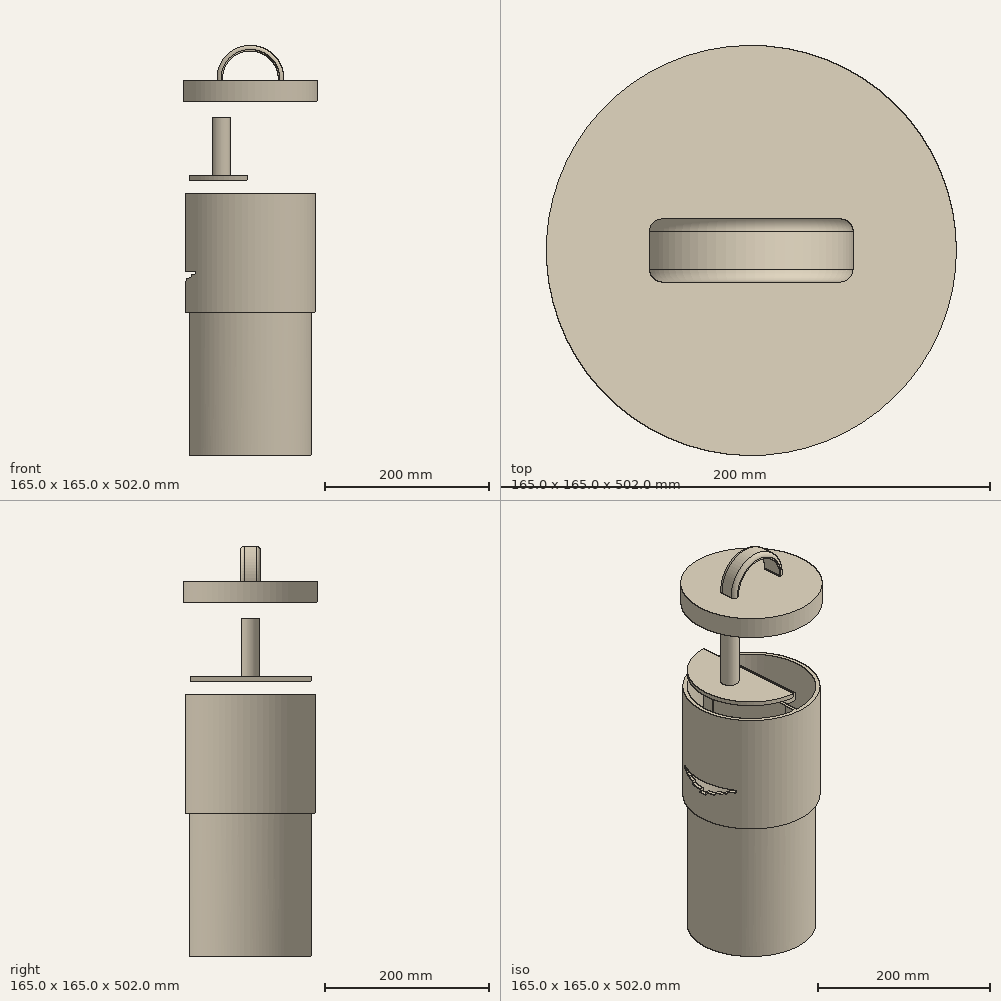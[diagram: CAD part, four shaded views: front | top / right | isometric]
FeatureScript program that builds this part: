
annotation { "Feature Type Name" : "Feature", "Feature Type Description" : "" }
export const myFeature = defineFeature(function(context is Context, id is Id, definition is map)
    precondition{}
    {
        {
            var Q0;
            Q0=qCreatedBy(makeId("Top.planeOp"),FACE);
            var sketch = newSketch(context, id + "F0", { "sketchPlane" : qUnion([Q0])});
            skCircle(sketch, "E0", {"center": v(0, 0) * mm, "radius": 75 * mm});
            skCircle(sketch, "E1", {"center": v(0, 0) * mm, "radius": 70 * mm});
            skSolve(sketch);
        }
        {
            var Q0;
            Q0 = qSketchRegion(id + "F0", true);
            extrude(context, id + "F1", {"entities" : qUnion([Q0]), "oppositeDirection" : true, "depth" : 200 * mm, "offsetDistance" : 25.4 * mm});
        }
        {
            var Q0;
            Q0=makeQuery(id+"F1.opExtrude","CAP_FACE",FACE,{"disambiguationData":[OSD([sQuery(id+"F0.wireOp",EDGE,"E0"),sQuery(id+"F0.wireOp",EDGE,"E1")])],"isStart":false});
            var sketch = newSketch(context, id + "F2", { "sketchPlane" : qUnion([Q0])});
            skCircle(sketch, "E2", {"center": v(0, 0) * mm, "radius": 75 * mm});
            skSolve(sketch);
        }
        {
            var Q0;
            Q0 = qSketchRegion(id + "F2", true);
            extrude(context, id + "F3", {"entities" : qUnion([Q0]), "operationType" : NewBodyOperationType.ADD, "oppositeDirection" : true, "depth" : 5 * mm, "offsetDistance" : 25.4 * mm});
        }
        {
            var Q0;
            Q0=qCreatedBy(makeId("Top.planeOp"),FACE);
            var sketch = newSketch(context, id + "F4", { "sketchPlane" : qUnion([Q0])});
            skCircle(sketch, "E3", {"center": v(0, 0) * mm, "radius": 80 * mm});
            skCircle(sketch, "E4", {"center": v(0, 0) * mm, "radius": 75 * mm});
            skSolve(sketch);
        }
        {
            var Q0;
            Q0 = qSketchRegion(id + "F4", true);
            extrude(context, id + "F5", {"entities" : qUnion([Q0]), "endBound" : BoundingType.SYMMETRIC, "oppositeDirection" : true, "depth" : 50.8 * mm, "offsetDistance" : 25.4 * mm});
        }
        {
            var Q0;
            Q0=qCreatedBy(makeId("Top.planeOp"),FACE);
            cPlane(context, id + "F6", {"entities" : qUnion([Q0]), "cplaneType" : CPlaneType.OFFSET, "offset" : 25.4 * mm, "width" : 152.4 * mm, "height" : 152.4 * mm});
        }
        {
            var Q0;
            Q0=qCreatedBy(makeId("Front.planeOp"),FACE);
            var sketch = newSketch(context, id + "F7", { "sketchPlane" : qUnion([Q0])});
            skLineSegment(sketch, "E5", {"start": v(-80, 0) * mm, "end": v(-7.87, 25.35) * mm});
            skLineSegment(sketch, "E6", {"start": v(-80, 0) * mm, "end": v(-80, 52.45) * mm, "construction": true});
            skSolve(sketch);
        }
        {
            var Q0;
            Q0 = qSketchRegion(id + "F7", true);
            var Q1;
            Q1=sQuery(id+"F7.wireOp",EDGE,"E5");
            var Q2;
            Q2=sQuery(id+"F7.wireOp",EDGE,"E6");
            revolve(context, id + "F8", {"bodyType" : ToolBodyType.SURFACE, "entities" : qUnion([Q0]), "surfaceEntities" : qUnion([Q1]), "axis" : qUnion([Q2]), "revolveType" : RevolveType.SYMMETRIC, "angle" : 130 * degree});
        }
        {
            var Q0;
            Q0=makeQuery(id+"F5.opExtrude","CAP_FACE",FACE,{"disambiguationData":[OSD([sQuery(id+"F4.wireOp",EDGE,"E3"),sQuery(id+"F4.wireOp",EDGE,"E4")])],"isStart":true});
            var sketch = newSketch(context, id + "F9", { "sketchPlane" : qUnion([Q0])});
            skLineSegment(sketch, "E7.bottom", {"start": v(-86.8, 42.34) * mm, "end": v(-65.14, 42.34) * mm});
            skLineSegment(sketch, "E7.top", {"start": v(-86.8, 5.69) * mm, "end": v(-65.14, 5.69) * mm});
            skLineSegment(sketch, "E7.left", {"start": v(-86.8, 42.34) * mm, "end": v(-86.8, 5.69) * mm});
            skLineSegment(sketch, "E7.right", {"start": v(-65.14, 42.34) * mm, "end": v(-65.14, 5.69) * mm});
            skLineSegment(sketch, "E8.bottom", {"start": v(-86.8, 5.87) * mm, "end": v(-65.14, 5.87) * mm});
            skLineSegment(sketch, "E8.top", {"start": v(-86.8, -42.97) * mm, "end": v(-65.14, -42.97) * mm});
            skLineSegment(sketch, "E8.left", {"start": v(-86.8, 5.87) * mm, "end": v(-86.8, -42.97) * mm});
            skLineSegment(sketch, "E8.right", {"start": v(-65.14, 5.87) * mm, "end": v(-65.14, -42.97) * mm});
            skSolve(sketch);
        }
        {
            var Q0;
            Q0 = qSketchRegion(id + "F9", true);
            extrude(context, id + "F10", {"entities" : qUnion([Q0]), "operationType" : NewBodyOperationType.REMOVE, "oppositeDirection" : true, "depth" : 3.56 * mm, "offsetDistance" : 25.4 * mm});
        }
        {
            var Q0;
            Q0=makeQuery(id+"F10.boolean.opBoolean","COPY",FACE,{"derivedFrom":makeQuery(id+"F10.opExtrude","CAP_FACE",FACE,{"disambiguationData":[OSD([sQuery(id+"F9.wireOp",EDGE,"E7.bottom"),sQuery(id+"F9.wireOp",EDGE,"E7.left"),sQuery(id+"F9.wireOp",EDGE,"E7.right"),sQuery(id+"F9.wireOp",EDGE,"E8.top"),sQuery(id+"F9.wireOp",EDGE,"E8.left"),sQuery(id+"F9.wireOp",EDGE,"E8.right")])],"isStart":false})});
            var sketch = newSketch(context, id + "F11", { "sketchPlane" : qUnion([Q0])});
            skLineSegment(sketch, "E9.bottom", {"start": v(-90.9, 34.1) * mm, "end": v(-64.9, 34.1) * mm});
            skLineSegment(sketch, "E9.top", {"start": v(-90.9, -33.56) * mm, "end": v(-64.9, -33.56) * mm});
            skLineSegment(sketch, "E9.left", {"start": v(-90.9, 34.1) * mm, "end": v(-90.9, -33.56) * mm});
            skLineSegment(sketch, "E9.right", {"start": v(-64.9, 34.1) * mm, "end": v(-64.9, -33.56) * mm});
            skSolve(sketch);
        }
        {
            var Q0;
            Q0 = qSketchRegion(id + "F11", true);
            extrude(context, id + "F12", {"entities" : qUnion([Q0]), "operationType" : NewBodyOperationType.REMOVE, "oppositeDirection" : true, "depth" : 3.3 * mm, "offsetDistance" : 25.4 * mm});
        }
        {
            var Q0;
            Q0=makeQuery(id+"F12.boolean.opBoolean","COPY",FACE,{"derivedFrom":makeQuery(id+"F12.opExtrude","CAP_FACE",FACE,{"disambiguationData":[OSD([sQuery(id+"F11.wireOp",EDGE,"E9.bottom"),sQuery(id+"F11.wireOp",EDGE,"E9.top"),sQuery(id+"F11.wireOp",EDGE,"E9.left"),sQuery(id+"F11.wireOp",EDGE,"E9.right")])],"isStart":false})});
            var sketch = newSketch(context, id + "F13", { "sketchPlane" : qUnion([Q0])});
            skLineSegment(sketch, "E10.bottom", {"start": v(-91.14, 27.35) * mm, "end": v(-66.34, 27.35) * mm});
            skLineSegment(sketch, "E10.top", {"start": v(-91.14, -28.5) * mm, "end": v(-66.34, -28.5) * mm});
            skLineSegment(sketch, "E10.left", {"start": v(-91.14, 27.35) * mm, "end": v(-91.14, -28.5) * mm});
            skLineSegment(sketch, "E10.right", {"start": v(-66.34, 27.35) * mm, "end": v(-66.34, -28.5) * mm});
            skSolve(sketch);
        }
        {
            var Q0;
            Q0 = qSketchRegion(id + "F13", true);
            extrude(context, id + "F14", {"entities" : qUnion([Q0]), "operationType" : NewBodyOperationType.REMOVE, "oppositeDirection" : true, "depth" : 2.03 * mm, "offsetDistance" : 25.4 * mm});
        }
        {
            var Q0;
            Q0=makeQuery(id+"F14.boolean.opBoolean","COPY",FACE,{"derivedFrom":makeQuery(id+"F14.opExtrude","CAP_FACE",FACE,{"disambiguationData":[OSD([sQuery(id+"F13.wireOp",EDGE,"E10.bottom"),sQuery(id+"F13.wireOp",EDGE,"E10.top"),sQuery(id+"F13.wireOp",EDGE,"E10.left"),sQuery(id+"F13.wireOp",EDGE,"E10.right")])],"isStart":false})});
            var sketch = newSketch(context, id + "F15", { "sketchPlane" : qUnion([Q0])});
            skLineSegment(sketch, "E11.bottom", {"start": v(-69.15, 4.9) * mm, "end": v(-89.84, 4.9) * mm});
            skLineSegment(sketch, "E11.top", {"start": v(-69.15, -4.83) * mm, "end": v(-89.84, -4.83) * mm});
            skLineSegment(sketch, "E11.left", {"start": v(-69.15, 4.9) * mm, "end": v(-69.15, -4.83) * mm});
            skLineSegment(sketch, "E11.right", {"start": v(-89.84, 4.9) * mm, "end": v(-89.84, -4.83) * mm});
            skSolve(sketch);
        }
        {
            var Q0;
            Q0 = qSketchRegion(id + "F15", true);
            extrude(context, id + "F16", {"entities" : qUnion([Q0]), "operationType" : NewBodyOperationType.REMOVE, "oppositeDirection" : true, "depth" : 7.87 * mm, "offsetDistance" : 25.4 * mm});
        }
        {
            var Q0;
            Q0=makeQuery(id+"F8.opRevolve","CAP_EDGE",EDGE,{"disambiguationData":[OSD([sQuery(id+"F7.wireOp",EDGE,"E5")])],"isStart":true});
            cPlane(context, id + "F17", {"entities" : qUnion([Q0]), "cplaneType" : CPlaneType.LINE_ANGLE, "offset" : 25.4 * mm, "angle" : 165 * degree, "oppositeDirection" : true, "width" : 152.4 * mm, "height" : 152.4 * mm});
        }
        {
            var Q0;
            {var subQ0=sQuery(id+"F13.wireOp",EDGE,"E10.bottom");Q0=makeQuery(id+"F16.boolean.opBoolean","SPLIT",FACE,{"disambiguationData":[TD([makeQuery(id+"F14.boolean.opBoolean","COPY",FACE,{"derivedFrom":makeQuery(id+"F14.opExtrude","SWEPT_FACE",FACE,{"disambiguationData":[OSD([subQ0])]})})])],"derivedFrom":makeQuery(id+"F14.boolean.opBoolean","COPY",FACE,{"derivedFrom":makeQuery(id+"F14.opExtrude","CAP_FACE",FACE,{"disambiguationData":[OSD([subQ0,sQuery(id+"F13.wireOp",EDGE,"E10.top"),sQuery(id+"F13.wireOp",EDGE,"E10.left"),sQuery(id+"F13.wireOp",EDGE,"E10.right")])],"isStart":false})})});}
            var sketch = newSketch(context, id + "F18", { "sketchPlane" : qUnion([Q0])});
            skLineSegment(sketch, "E12.bottom", {"start": v(-90.52, 19.85) * mm, "end": v(-62.11, 19.85) * mm});
            skLineSegment(sketch, "E12.top", {"start": v(-90.52, -19) * mm, "end": v(-62.11, -19) * mm});
            skLineSegment(sketch, "E12.left", {"start": v(-90.52, 19.85) * mm, "end": v(-90.52, -19) * mm});
            skLineSegment(sketch, "E12.right", {"start": v(-62.11, 19.85) * mm, "end": v(-62.11, -19) * mm});
            skSolve(sketch);
        }
        {
            var Q0;
            Q0 = qSketchRegion(id + "F18", true);
            extrude(context, id + "F19", {"entities" : qUnion([Q0]), "operationType" : NewBodyOperationType.REMOVE, "oppositeDirection" : true, "depth" : 3.8 * mm, "offsetDistance" : 25.4 * mm});
        }
        {
            var Q0;
            {var subQ0=makeQuery(id+"F5.opExtrude","SWEPT_FACE",FACE,{"disambiguationData":[OSD([sQuery(id+"F4.wireOp",EDGE,"E3")])]});var subQ1=sQuery(id+"F9.wireOp",EDGE,"E8.top");var subQ2=makeQuery(id+"F10.opExtrude","CAP_FACE",FACE,{"disambiguationData":[OSD([sQuery(id+"F9.wireOp",EDGE,"E7.bottom"),sQuery(id+"F9.wireOp",EDGE,"E7.left"),sQuery(id+"F9.wireOp",EDGE,"E7.right"),subQ1,sQuery(id+"F9.wireOp",EDGE,"E8.left"),sQuery(id+"F9.wireOp",EDGE,"E8.right")])],"isStart":false});Q0=makeQuery(id+"F12.boolean.opBoolean","SPLIT",EDGE,{"disambiguationData":[TD([makeQuery(id+"F10.boolean.opBoolean","COPY",FACE,{"derivedFrom":makeQuery(id+"F10.opExtrude","SWEPT_FACE",FACE,{"disambiguationData":[OSD([subQ1])]})})])],"derivedFrom":makeQuery(id+"F10.boolean.opBoolean","INTERSECT",EDGE,{"derivedFrom":[subQ0,subQ2]})});}
            var Q1;
            {var subQ0=makeQuery(id+"F5.opExtrude","SWEPT_FACE",FACE,{"disambiguationData":[OSD([sQuery(id+"F4.wireOp",EDGE,"E3")])]});var subQ1=sQuery(id+"F11.wireOp",EDGE,"E9.top");var subQ2=makeQuery(id+"F12.opExtrude","CAP_FACE",FACE,{"disambiguationData":[OSD([sQuery(id+"F11.wireOp",EDGE,"E9.bottom"),subQ1,sQuery(id+"F11.wireOp",EDGE,"E9.left"),sQuery(id+"F11.wireOp",EDGE,"E9.right")])],"isStart":false});Q1=makeQuery(id+"F14.boolean.opBoolean","SPLIT",EDGE,{"disambiguationData":[TD([makeQuery(id+"F12.boolean.opBoolean","COPY",FACE,{"derivedFrom":makeQuery(id+"F12.opExtrude","SWEPT_FACE",FACE,{"disambiguationData":[OSD([subQ1])]})})])],"derivedFrom":makeQuery(id+"F12.boolean.opBoolean","INTERSECT",EDGE,{"derivedFrom":[subQ0,subQ2]})});}
            var Q2;
            {var subQ0=makeQuery(id+"F5.opExtrude","SWEPT_FACE",FACE,{"disambiguationData":[OSD([sQuery(id+"F4.wireOp",EDGE,"E3")])]});var subQ1=sQuery(id+"F13.wireOp",EDGE,"E10.top");var subQ2=makeQuery(id+"F14.opExtrude","CAP_FACE",FACE,{"disambiguationData":[OSD([sQuery(id+"F13.wireOp",EDGE,"E10.bottom"),subQ1,sQuery(id+"F13.wireOp",EDGE,"E10.left"),sQuery(id+"F13.wireOp",EDGE,"E10.right")])],"isStart":false});Q2=makeQuery(id+"F16.boolean.opBoolean","SPLIT",EDGE,{"disambiguationData":[TD([makeQuery(id+"F14.boolean.opBoolean","COPY",FACE,{"derivedFrom":makeQuery(id+"F14.opExtrude","SWEPT_FACE",FACE,{"disambiguationData":[OSD([subQ1])]})})])],"derivedFrom":makeQuery(id+"F14.boolean.opBoolean","INTERSECT",EDGE,{"derivedFrom":[subQ0,subQ2]})});}
            var Q3;
            Q3=makeQuery(id+"F19.boolean.opBoolean","INTERSECT",EDGE,{"disambiguationData":[OD(1.0)],"derivedFrom":[makeQuery(id+"F5.opExtrude","SWEPT_FACE",FACE,{"disambiguationData":[OSD([sQuery(id+"F4.wireOp",EDGE,"E3")])]}),makeQuery(id+"F19.opExtrude","CAP_FACE",FACE,{"disambiguationData":[OSD([sQuery(id+"F18.wireOp",EDGE,"E12.bottom"),sQuery(id+"F18.wireOp",EDGE,"E12.top"),sQuery(id+"F18.wireOp",EDGE,"E12.left"),sQuery(id+"F18.wireOp",EDGE,"E12.right")])],"isStart":false})]});
            var Q4;
            {var subQ0=makeQuery(id+"F5.opExtrude","SWEPT_FACE",FACE,{"disambiguationData":[OSD([sQuery(id+"F4.wireOp",EDGE,"E4")])]});var subQ1=sQuery(id+"F13.wireOp",EDGE,"E10.top");var subQ2=makeQuery(id+"F14.opExtrude","CAP_FACE",FACE,{"disambiguationData":[OSD([sQuery(id+"F13.wireOp",EDGE,"E10.bottom"),subQ1,sQuery(id+"F13.wireOp",EDGE,"E10.left"),sQuery(id+"F13.wireOp",EDGE,"E10.right")])],"isStart":false});Q4=makeQuery(id+"F16.boolean.opBoolean","SPLIT",EDGE,{"disambiguationData":[TD([makeQuery(id+"F14.boolean.opBoolean","COPY",FACE,{"derivedFrom":makeQuery(id+"F14.opExtrude","SWEPT_FACE",FACE,{"disambiguationData":[OSD([subQ1])]})})])],"derivedFrom":makeQuery(id+"F14.boolean.opBoolean","INTERSECT",EDGE,{"derivedFrom":[subQ0,subQ2]})});}
            var Q5;
            {var subQ0=makeQuery(id+"F5.opExtrude","SWEPT_FACE",FACE,{"disambiguationData":[OSD([sQuery(id+"F4.wireOp",EDGE,"E4")])]});var subQ1=sQuery(id+"F11.wireOp",EDGE,"E9.top");var subQ2=makeQuery(id+"F12.opExtrude","CAP_FACE",FACE,{"disambiguationData":[OSD([sQuery(id+"F11.wireOp",EDGE,"E9.bottom"),subQ1,sQuery(id+"F11.wireOp",EDGE,"E9.left"),sQuery(id+"F11.wireOp",EDGE,"E9.right")])],"isStart":false});Q5=makeQuery(id+"F14.boolean.opBoolean","SPLIT",EDGE,{"disambiguationData":[TD([makeQuery(id+"F12.boolean.opBoolean","COPY",FACE,{"derivedFrom":makeQuery(id+"F12.opExtrude","SWEPT_FACE",FACE,{"disambiguationData":[OSD([subQ1])]})})])],"derivedFrom":makeQuery(id+"F12.boolean.opBoolean","INTERSECT",EDGE,{"derivedFrom":[subQ0,subQ2]})});}
            var Q6;
            {var subQ0=sQuery(id+"F4.wireOp",EDGE,"E4");var subQ1=makeQuery(id+"F5.opExtrude","SWEPT_FACE",FACE,{"disambiguationData":[OSD([subQ0])]});var subQ2=sQuery(id+"F9.wireOp",EDGE,"E8.right");var subQ3=sQuery(id+"F9.wireOp",EDGE,"E8.top");var subQ4=sQuery(id+"F9.wireOp",EDGE,"E7.right");var subQ5=makeQuery(id+"F10.opExtrude","CAP_FACE",FACE,{"disambiguationData":[OSD([sQuery(id+"F9.wireOp",EDGE,"E7.bottom"),sQuery(id+"F9.wireOp",EDGE,"E7.left"),subQ4,subQ3,sQuery(id+"F9.wireOp",EDGE,"E8.left"),subQ2])],"isStart":false});Q6=makeQuery(id+"F12.boolean.opBoolean","SPLIT",EDGE,{"disambiguationData":[TD([makeQuery(id+"F12.opExtrude","SWEPT_FACE",FACE,{"disambiguationData":[OSD([sQuery(id+"F11.wireOp",EDGE,"E9.top")])]})])],"derivedFrom":makeQuery(id+"F10.boolean.opBoolean","INTERSECT",EDGE,{"derivedFrom":[subQ1,subQ5]})});}
            var Q7;
            Q7=makeQuery(id+"F12.boolean.opBoolean","COPY",EDGE,{"derivedFrom":makeQuery(id+"F12.opExtrude","CAP_EDGE",EDGE,{"disambiguationData":[OSD([sQuery(id+"F11.wireOp",EDGE,"E9.top")])],"isStart":true})});
            var Q8;
            Q8=makeQuery(id+"F14.boolean.opBoolean","COPY",EDGE,{"derivedFrom":makeQuery(id+"F14.opExtrude","CAP_EDGE",EDGE,{"disambiguationData":[OSD([sQuery(id+"F13.wireOp",EDGE,"E10.top")])],"isStart":true})});
            var Q9;
            Q9=makeQuery(id+"F19.boolean.opBoolean","COPY",EDGE,{"derivedFrom":makeQuery(id+"F19.opExtrude","CAP_EDGE",EDGE,{"disambiguationData":[OSD([sQuery(id+"F18.wireOp",EDGE,"E12.top")])],"isStart":true})});
            var Q10;
            Q10=makeQuery(id+"F19.boolean.opBoolean","INTERSECT",EDGE,{"disambiguationData":[OD(1.0)],"derivedFrom":[makeQuery(id+"F5.opExtrude","SWEPT_FACE",FACE,{"disambiguationData":[OSD([sQuery(id+"F4.wireOp",EDGE,"E4")])]}),makeQuery(id+"F19.opExtrude","CAP_FACE",FACE,{"disambiguationData":[OSD([sQuery(id+"F18.wireOp",EDGE,"E12.bottom"),sQuery(id+"F18.wireOp",EDGE,"E12.top"),sQuery(id+"F18.wireOp",EDGE,"E12.left"),sQuery(id+"F18.wireOp",EDGE,"E12.right")])],"isStart":false})]});
            var Q11;
            Q11=makeQuery(id+"F19.boolean.opBoolean","INTERSECT",EDGE,{"derivedFrom":[makeQuery(id+"F16.boolean.opBoolean","COPY",FACE,{"derivedFrom":makeQuery(id+"F16.opExtrude","SWEPT_FACE",FACE,{"disambiguationData":[OSD([sQuery(id+"F15.wireOp",EDGE,"E11.top")])]})}),makeQuery(id+"F19.opExtrude","CAP_FACE",FACE,{"disambiguationData":[OSD([sQuery(id+"F18.wireOp",EDGE,"E12.bottom"),sQuery(id+"F18.wireOp",EDGE,"E12.top"),sQuery(id+"F18.wireOp",EDGE,"E12.left"),sQuery(id+"F18.wireOp",EDGE,"E12.right")])],"isStart":false})]});
            var Q12;
            Q12=makeQuery(id+"F16.boolean.opBoolean","COPY",FACE,{"derivedFrom":makeQuery(id+"F16.opExtrude","CAP_FACE",FACE,{"disambiguationData":[OSD([sQuery(id+"F15.wireOp",EDGE,"E11.bottom"),sQuery(id+"F15.wireOp",EDGE,"E11.top"),sQuery(id+"F15.wireOp",EDGE,"E11.left"),sQuery(id+"F15.wireOp",EDGE,"E11.right")])],"isStart":false})});
            var Q13;
            {var subQ0=sQuery(id+"F18.wireOp",EDGE,"E12.bottom");Q13=makeQuery(id+"F19.boolean.opBoolean","COPY",FACE,{"disambiguationData":[TD([makeQuery(id+"F16.boolean.opBoolean","COPY",FACE,{"derivedFrom":makeQuery(id+"F16.opExtrude","SWEPT_FACE",FACE,{"disambiguationData":[OSD([sQuery(id+"F15.wireOp",EDGE,"E11.bottom")])]})})])],"derivedFrom":makeQuery(id+"F19.opExtrude","CAP_FACE",FACE,{"disambiguationData":[OSD([subQ0,sQuery(id+"F18.wireOp",EDGE,"E12.top"),sQuery(id+"F18.wireOp",EDGE,"E12.left"),sQuery(id+"F18.wireOp",EDGE,"E12.right")])],"isStart":false})});}
            var Q14;
            {var subQ0=sQuery(id+"F13.wireOp",EDGE,"E10.bottom");Q14=makeQuery(id+"F16.boolean.opBoolean","SPLIT",FACE,{"disambiguationData":[TD([makeQuery(id+"F14.boolean.opBoolean","COPY",FACE,{"derivedFrom":makeQuery(id+"F14.opExtrude","SWEPT_FACE",FACE,{"disambiguationData":[OSD([subQ0])]})})])],"derivedFrom":makeQuery(id+"F14.boolean.opBoolean","COPY",FACE,{"derivedFrom":makeQuery(id+"F14.opExtrude","CAP_FACE",FACE,{"disambiguationData":[OSD([subQ0,sQuery(id+"F13.wireOp",EDGE,"E10.top"),sQuery(id+"F13.wireOp",EDGE,"E10.left"),sQuery(id+"F13.wireOp",EDGE,"E10.right")])],"isStart":false})})});}
            var Q15;
            {var subQ0=sQuery(id+"F11.wireOp",EDGE,"E9.bottom");Q15=makeQuery(id+"F14.boolean.opBoolean","SPLIT",FACE,{"disambiguationData":[TD([makeQuery(id+"F12.boolean.opBoolean","COPY",FACE,{"derivedFrom":makeQuery(id+"F12.opExtrude","SWEPT_FACE",FACE,{"disambiguationData":[OSD([subQ0])]})})])],"derivedFrom":makeQuery(id+"F12.boolean.opBoolean","COPY",FACE,{"derivedFrom":makeQuery(id+"F12.opExtrude","CAP_FACE",FACE,{"disambiguationData":[OSD([subQ0,sQuery(id+"F11.wireOp",EDGE,"E9.top"),sQuery(id+"F11.wireOp",EDGE,"E9.left"),sQuery(id+"F11.wireOp",EDGE,"E9.right")])],"isStart":false})})});}
            var Q16;
            {var subQ0=sQuery(id+"F9.wireOp",EDGE,"E7.bottom");var subQ1=makeQuery(id+"F10.opExtrude","SWEPT_FACE",FACE,{"disambiguationData":[OSD([subQ0])]});var subQ5=sQuery(id+"F9.wireOp",EDGE,"E8.right");var subQ6=sQuery(id+"F9.wireOp",EDGE,"E7.right");var subQ7=makeQuery(id+"F10.opExtrude","CAP_FACE",FACE,{"disambiguationData":[OSD([subQ0,sQuery(id+"F9.wireOp",EDGE,"E7.left"),subQ6,sQuery(id+"F9.wireOp",EDGE,"E8.top"),sQuery(id+"F9.wireOp",EDGE,"E8.left"),subQ5])],"isStart":false});Q16=makeQuery(id+"F12.boolean.opBoolean","SPLIT",FACE,{"disambiguationData":[TD([makeQuery(id+"F10.boolean.opBoolean","COPY",FACE,{"derivedFrom":subQ1})])],"derivedFrom":makeQuery(id+"F10.boolean.opBoolean","COPY",FACE,{"derivedFrom":subQ7})});}
            fillet(context, id + "F20", {"entities" : qUnion([Q0, Q1, Q2, Q3, Q4, Q5, Q6, Q7, Q8, Q9, Q10, Q11, Q12, Q13, Q14, Q15, Q16]), "radius" : 0.25 * mm, "tangentPropagation" : true, "allowEdgeOverflow" : false});
        }
        {
            var Q0;
            Q0=qCreatedBy(id+"F6.planeOp",FACE);
            var sketch = newSketch(context, id + "F21", { "sketchPlane" : qUnion([Q0])});
            skCircle(sketch, "E13", {"center": v(0, 0) * mm, "radius": 80 * mm});
            skCircle(sketch, "E14", {"center": v(-46.54, 49.13) * mm, "radius": 2.19 * mm});
            skCircle(sketch, "E15", {"center": v(-43.94, 41.98) * mm, "radius": 2.19 * mm});
            skCircle(sketch, "E16", {"center": v(-67, 0) * mm, "radius": 2.19 * mm});
            skCircle(sketch, "E17", {"center": v(-52.1, 39.38) * mm, "radius": 2.19 * mm});
            skCircle(sketch, "E18", {"center": v(-38.89, 50.38) * mm, "radius": 2.19 * mm});
            skCircle(sketch, "E19", {"center": v(-29.2, 45.54) * mm, "radius": 2.19 * mm});
            skCircle(sketch, "E20", {"center": v(-34.93, 41.58) * mm, "radius": 2.19 * mm});
            skCircle(sketch, "E21", {"center": v(-22.6, 37.18) * mm, "radius": 2.19 * mm});
            skCircle(sketch, "E22", {"center": v(-30.97, 34.54) * mm, "radius": 2.19 * mm});
            skCircle(sketch, "E23", {"center": v(-39.33, 33.22) * mm, "radius": 2.19 * mm});
            skCircle(sketch, "E24", {"center": v(-49.01, 32.78) * mm, "radius": 2.19 * mm});
            skCircle(sketch, "E25", {"center": v(-55.62, 32.34) * mm, "radius": 2.19 * mm});
            skCircle(sketch, "E26", {"center": v(-63.1, 29.7) * mm, "radius": 2.19 * mm});
            skCircle(sketch, "E27", {"center": v(-65.74, 20.9) * mm, "radius": 2.19 * mm});
            skCircle(sketch, "E28", {"center": v(-67.5, 14.73) * mm, "radius": 2.19 * mm});
            skCircle(sketch, "E29", {"center": v(-60.02, 8.56) * mm, "radius": 2.19 * mm});
            skCircle(sketch, "E30", {"center": v(-59.14, 18.25) * mm, "radius": 2.19 * mm});
            skCircle(sketch, "E31", {"center": v(-53.86, 24.85) * mm, "radius": 2.19 * mm});
            skCircle(sketch, "E32", {"center": v(-44.17, 23.1) * mm, "radius": 2.19 * mm});
            skCircle(sketch, "E33", {"center": v(-33.17, 27.5) * mm, "radius": 2.19 * mm});
            skCircle(sketch, "E34", {"center": v(-25.24, 28.37) * mm, "radius": 2.19 * mm});
            skCircle(sketch, "E35", {"center": v(-17.76, 27.5) * mm, "radius": 2.19 * mm});
            skCircle(sketch, "E36", {"center": v(-15.12, 17.8) * mm, "radius": 2.19 * mm});
            skCircle(sketch, "E37", {"center": v(-23.92, 18.25) * mm, "radius": 2.19 * mm});
            skCircle(sketch, "E38", {"center": v(-32.29, 16.93) * mm, "radius": 2.19 * mm});
            skCircle(sketch, "E39", {"center": v(-37.57, 16.93) * mm, "radius": 2.19 * mm});
            skCircle(sketch, "E40", {"center": v(-49.45, 15.6) * mm, "radius": 2.19 * mm});
            skCircle(sketch, "E41", {"center": v(-50.78, 8.12) * mm, "radius": 2.19 * mm});
            skCircle(sketch, "E42", {"center": v(-40.65, 9.88) * mm, "radius": 2.19 * mm});
            skCircle(sketch, "E43", {"center": v(-30.53, 7.68) * mm, "radius": 2.19 * mm});
            skCircle(sketch, "E44", {"center": v(-24.8, 9) * mm, "radius": 2.19 * mm});
            skCircle(sketch, "E45", {"center": v(-16, 9) * mm, "radius": 2.19 * mm});
            skCircle(sketch, "E46", {"center": v(-11.6, 1.96) * mm, "radius": 2.19 * mm});
            skCircle(sketch, "E47", {"center": v(-18.2, 2.4) * mm, "radius": 2.19 * mm});
            skCircle(sketch, "E48", {"center": v(-28.76, 2.84) * mm, "radius": 2.19 * mm});
            skCircle(sketch, "E49", {"center": v(-37.57, 2.4) * mm, "radius": 2.19 * mm});
            skCircle(sketch, "E50", {"center": v(-45.05, 1.52) * mm, "radius": 2.19 * mm});
            skCircle(sketch, "E51", {"center": v(-56.06, 1.96) * mm, "radius": 2.19 * mm});
            skCircle(sketch, "E52", {"center": v(-70.58, 7.24) * mm, "radius": 2.19 * mm});
            skCircle(sketch, "E53", {"center": v(-68.38, -7.72) * mm, "radius": 2.19 * mm});
            skCircle(sketch, "E54", {"center": v(-66.62, -15.65) * mm, "radius": 2.19 * mm});
            skCircle(sketch, "E55", {"center": v(-64.42, -24.9) * mm, "radius": 2.19 * mm});
            skCircle(sketch, "E56", {"center": v(-59.58, -31.06) * mm, "radius": 2.19 * mm});
            skCircle(sketch, "E57", {"center": v(-56.94, -37.66) * mm, "radius": 2.19 * mm});
            skCircle(sketch, "E58", {"center": v(-53.42, -46.02) * mm, "radius": 2.19 * mm});
            skCircle(sketch, "E59", {"center": v(-45.93, -50.87) * mm, "radius": 2.19 * mm});
            skCircle(sketch, "E60", {"center": v(-34.49, -49.99) * mm, "radius": 2.19 * mm});
            skCircle(sketch, "E61", {"center": v(-30.08, -43.82) * mm, "radius": 2.19 * mm});
            skCircle(sketch, "E62", {"center": v(-22.16, -34.58) * mm, "radius": 2.19 * mm});
            skCircle(sketch, "E63", {"center": v(-16, -24.01) * mm, "radius": 2.19 * mm});
            skCircle(sketch, "E64", {"center": v(-12.48, -14.33) * mm, "radius": 2.19 * mm});
            skCircle(sketch, "E65", {"center": v(-10.27, -7.72) * mm, "radius": 2.19 * mm});
            skCircle(sketch, "E66", {"center": v(-21.72, -4.2) * mm, "radius": 2.19 * mm});
            skCircle(sketch, "E67", {"center": v(-23.04, -13.45) * mm, "radius": 2.19 * mm});
            skCircle(sketch, "E68", {"center": v(-23.48, -20.5) * mm, "radius": 2.19 * mm});
            skCircle(sketch, "E69", {"center": v(-25.68, -26.65) * mm, "radius": 2.19 * mm});
            skCircle(sketch, "E70", {"center": v(-31.85, -33.7) * mm, "radius": 2.19 * mm});
            skCircle(sketch, "E71", {"center": v(-37.57, -38.98) * mm, "radius": 2.19 * mm});
            skCircle(sketch, "E72", {"center": v(-42.41, -42.06) * mm, "radius": 2.19 * mm});
            skCircle(sketch, "E73", {"center": v(-47.7, -33.26) * mm, "radius": 2.19 * mm});
            skCircle(sketch, "E74", {"center": v(-51.66, -26.21) * mm, "radius": 2.19 * mm});
            skCircle(sketch, "E75", {"center": v(-53.86, -20.05) * mm, "radius": 2.19 * mm});
            skCircle(sketch, "E76", {"center": v(-56.5, -14.77) * mm, "radius": 2.19 * mm});
            skCircle(sketch, "E77", {"center": v(-56.06, -5.52) * mm, "radius": 2.19 * mm});
            skCircle(sketch, "E78", {"center": v(-47.25, -4.64) * mm, "radius": 2.19 * mm});
            skCircle(sketch, "E79", {"center": v(-35.8, -8.16) * mm, "radius": 2.19 * mm});
            skCircle(sketch, "E80", {"center": v(-41.53, -16.09) * mm, "radius": 2.19 * mm});
            skCircle(sketch, "E81", {"center": v(-44.17, -25.77) * mm, "radius": 2.19 * mm});
            skCircle(sketch, "E82", {"center": v(-47.7, -15.2) * mm, "radius": 2.19 * mm});
            skCircle(sketch, "E83", {"center": v(-26.56, -7.28) * mm, "radius": 2.19 * mm});
            skCircle(sketch, "E84", {"center": v(-31.4, -20.05) * mm, "radius": 2.19 * mm});
            skCircle(sketch, "E85", {"center": v(-36.25, -27.1) * mm, "radius": 2.19 * mm});
            skCircle(sketch, "E86", {"center": v(-31.01, -13.8) * mm, "radius": 2.19 * mm});
            skCircle(sketch, "E87", {"center": v(-33.1, -2.66) * mm, "radius": 2.19 * mm});
            skCircle(sketch, "E88", {"center": v(-43.42, -9.4) * mm, "radius": 2.19 * mm});
            skLineSegment(sketch, "E89.bottom", {"start": v(-3.76, -59.92) * mm, "end": v(28.21, -59.92) * mm});
            skLineSegment(sketch, "E89.top", {"start": v(-3.76, 59.85) * mm, "end": v(28.21, 59.85) * mm});
            skLineSegment(sketch, "E89.left", {"start": v(-3.76, -59.92) * mm, "end": v(-3.76, 59.85) * mm});
            skArc(sketch, "E90", {"start": v(28.21, -59.92) * mm, "mid": v(65.29, -0.04) * mm, "end": v(28.21, 59.85) * mm});
            skSolve(sketch);
        }
        {
            var Q0;
            Q0 = qSketchRegion(id + "F21", true);
            extrude(context, id + "F22", {"entities" : qUnion([Q0]), "operationType" : NewBodyOperationType.ADD, "depth" : 5 * mm, "offsetDistance" : 25.4 * mm});
        }
        {
            var Q0;
            Q0=makeQuery(id+"F22.opExtrude","CAP_FACE",FACE,{"disambiguationData":[OSD([sQuery(id+"F21.wireOp",EDGE,"E13"),sQuery(id+"F21.wireOp",EDGE,"E14"),sQuery(id+"F21.wireOp",EDGE,"E15"),sQuery(id+"F21.wireOp",EDGE,"E16"),sQuery(id+"F21.wireOp",EDGE,"E17"),sQuery(id+"F21.wireOp",EDGE,"E18"),sQuery(id+"F21.wireOp",EDGE,"E19"),sQuery(id+"F21.wireOp",EDGE,"E20"),sQuery(id+"F21.wireOp",EDGE,"E21"),sQuery(id+"F21.wireOp",EDGE,"E22"),sQuery(id+"F21.wireOp",EDGE,"E23"),sQuery(id+"F21.wireOp",EDGE,"E24"),sQuery(id+"F21.wireOp",EDGE,"E25"),sQuery(id+"F21.wireOp",EDGE,"E26"),sQuery(id+"F21.wireOp",EDGE,"E27"),sQuery(id+"F21.wireOp",EDGE,"E28"),sQuery(id+"F21.wireOp",EDGE,"E29"),sQuery(id+"F21.wireOp",EDGE,"E30"),sQuery(id+"F21.wireOp",EDGE,"E31"),sQuery(id+"F21.wireOp",EDGE,"E32"),sQuery(id+"F21.wireOp",EDGE,"E33"),sQuery(id+"F21.wireOp",EDGE,"E34"),sQuery(id+"F21.wireOp",EDGE,"E35"),sQuery(id+"F21.wireOp",EDGE,"E36"),sQuery(id+"F21.wireOp",EDGE,"E37"),sQuery(id+"F21.wireOp",EDGE,"E38"),sQuery(id+"F21.wireOp",EDGE,"E39"),sQuery(id+"F21.wireOp",EDGE,"E40"),sQuery(id+"F21.wireOp",EDGE,"E41"),sQuery(id+"F21.wireOp",EDGE,"E42"),sQuery(id+"F21.wireOp",EDGE,"E43"),sQuery(id+"F21.wireOp",EDGE,"E44"),sQuery(id+"F21.wireOp",EDGE,"E45"),sQuery(id+"F21.wireOp",EDGE,"E46"),sQuery(id+"F21.wireOp",EDGE,"E47"),sQuery(id+"F21.wireOp",EDGE,"E48"),sQuery(id+"F21.wireOp",EDGE,"E49"),sQuery(id+"F21.wireOp",EDGE,"E50"),sQuery(id+"F21.wireOp",EDGE,"E51"),sQuery(id+"F21.wireOp",EDGE,"E52"),sQuery(id+"F21.wireOp",EDGE,"E53"),sQuery(id+"F21.wireOp",EDGE,"E54"),sQuery(id+"F21.wireOp",EDGE,"E55"),sQuery(id+"F21.wireOp",EDGE,"E56"),sQuery(id+"F21.wireOp",EDGE,"E57"),sQuery(id+"F21.wireOp",EDGE,"E58"),sQuery(id+"F21.wireOp",EDGE,"E59"),sQuery(id+"F21.wireOp",EDGE,"E60"),sQuery(id+"F21.wireOp",EDGE,"E61"),sQuery(id+"F21.wireOp",EDGE,"E62"),sQuery(id+"F21.wireOp",EDGE,"E63"),sQuery(id+"F21.wireOp",EDGE,"E64"),sQuery(id+"F21.wireOp",EDGE,"E65"),sQuery(id+"F21.wireOp",EDGE,"E66"),sQuery(id+"F21.wireOp",EDGE,"E67"),sQuery(id+"F21.wireOp",EDGE,"E68"),sQuery(id+"F21.wireOp",EDGE,"E69"),sQuery(id+"F21.wireOp",EDGE,"E70"),sQuery(id+"F21.wireOp",EDGE,"E71"),sQuery(id+"F21.wireOp",EDGE,"E72"),sQuery(id+"F21.wireOp",EDGE,"E73"),sQuery(id+"F21.wireOp",EDGE,"E74"),sQuery(id+"F21.wireOp",EDGE,"E75"),sQuery(id+"F21.wireOp",EDGE,"E76"),sQuery(id+"F21.wireOp",EDGE,"E77"),sQuery(id+"F21.wireOp",EDGE,"E78"),sQuery(id+"F21.wireOp",EDGE,"E79"),sQuery(id+"F21.wireOp",EDGE,"E80"),sQuery(id+"F21.wireOp",EDGE,"E81"),sQuery(id+"F21.wireOp",EDGE,"E82"),sQuery(id+"F21.wireOp",EDGE,"E83"),sQuery(id+"F21.wireOp",EDGE,"E84"),sQuery(id+"F21.wireOp",EDGE,"E85"),sQuery(id+"F21.wireOp",EDGE,"E86"),sQuery(id+"F21.wireOp",EDGE,"E87"),sQuery(id+"F21.wireOp",EDGE,"E88"),sQuery(id+"F21.wireOp",EDGE,"E89.bottom"),sQuery(id+"F21.wireOp",EDGE,"E89.top"),sQuery(id+"F21.wireOp",EDGE,"E89.left"),sQuery(id+"F21.wireOp",EDGE,"E90")])],"isStart":false});
            var sketch = newSketch(context, id + "F23", { "sketchPlane" : qUnion([Q0])});
            skCircle(sketch, "E91", {"center": v(0, 0) * mm, "radius": 80 * mm});
            skCircle(sketch, "E92", {"center": v(0, 0) * mm, "radius": 75 * mm});
            skSolve(sketch);
        }
        {
            var Q0;
            Q0 = qSketchRegion(id + "F23", true);
            extrude(context, id + "F24", {"entities" : qUnion([Q0]), "operationType" : NewBodyOperationType.ADD, "depth" : 90 * mm, "offsetDistance" : 25.4 * mm});
        }
        {
            var Q0;
            Q0=makeQuery(id+"F22.opExtrude","CAP_FACE",FACE,{"disambiguationData":[OSD([sQuery(id+"F21.wireOp",EDGE,"E13"),sQuery(id+"F21.wireOp",EDGE,"E14"),sQuery(id+"F21.wireOp",EDGE,"E15"),sQuery(id+"F21.wireOp",EDGE,"E16"),sQuery(id+"F21.wireOp",EDGE,"E17"),sQuery(id+"F21.wireOp",EDGE,"E18"),sQuery(id+"F21.wireOp",EDGE,"E19"),sQuery(id+"F21.wireOp",EDGE,"E20"),sQuery(id+"F21.wireOp",EDGE,"E21"),sQuery(id+"F21.wireOp",EDGE,"E22"),sQuery(id+"F21.wireOp",EDGE,"E23"),sQuery(id+"F21.wireOp",EDGE,"E24"),sQuery(id+"F21.wireOp",EDGE,"E25"),sQuery(id+"F21.wireOp",EDGE,"E26"),sQuery(id+"F21.wireOp",EDGE,"E27"),sQuery(id+"F21.wireOp",EDGE,"E28"),sQuery(id+"F21.wireOp",EDGE,"E29"),sQuery(id+"F21.wireOp",EDGE,"E30"),sQuery(id+"F21.wireOp",EDGE,"E31"),sQuery(id+"F21.wireOp",EDGE,"E32"),sQuery(id+"F21.wireOp",EDGE,"E33"),sQuery(id+"F21.wireOp",EDGE,"E34"),sQuery(id+"F21.wireOp",EDGE,"E35"),sQuery(id+"F21.wireOp",EDGE,"E36"),sQuery(id+"F21.wireOp",EDGE,"E37"),sQuery(id+"F21.wireOp",EDGE,"E38"),sQuery(id+"F21.wireOp",EDGE,"E39"),sQuery(id+"F21.wireOp",EDGE,"E40"),sQuery(id+"F21.wireOp",EDGE,"E41"),sQuery(id+"F21.wireOp",EDGE,"E42"),sQuery(id+"F21.wireOp",EDGE,"E43"),sQuery(id+"F21.wireOp",EDGE,"E44"),sQuery(id+"F21.wireOp",EDGE,"E45"),sQuery(id+"F21.wireOp",EDGE,"E46"),sQuery(id+"F21.wireOp",EDGE,"E47"),sQuery(id+"F21.wireOp",EDGE,"E48"),sQuery(id+"F21.wireOp",EDGE,"E49"),sQuery(id+"F21.wireOp",EDGE,"E50"),sQuery(id+"F21.wireOp",EDGE,"E51"),sQuery(id+"F21.wireOp",EDGE,"E52"),sQuery(id+"F21.wireOp",EDGE,"E53"),sQuery(id+"F21.wireOp",EDGE,"E54"),sQuery(id+"F21.wireOp",EDGE,"E55"),sQuery(id+"F21.wireOp",EDGE,"E56"),sQuery(id+"F21.wireOp",EDGE,"E57"),sQuery(id+"F21.wireOp",EDGE,"E58"),sQuery(id+"F21.wireOp",EDGE,"E59"),sQuery(id+"F21.wireOp",EDGE,"E60"),sQuery(id+"F21.wireOp",EDGE,"E61"),sQuery(id+"F21.wireOp",EDGE,"E62"),sQuery(id+"F21.wireOp",EDGE,"E63"),sQuery(id+"F21.wireOp",EDGE,"E64"),sQuery(id+"F21.wireOp",EDGE,"E65"),sQuery(id+"F21.wireOp",EDGE,"E66"),sQuery(id+"F21.wireOp",EDGE,"E67"),sQuery(id+"F21.wireOp",EDGE,"E68"),sQuery(id+"F21.wireOp",EDGE,"E69"),sQuery(id+"F21.wireOp",EDGE,"E70"),sQuery(id+"F21.wireOp",EDGE,"E71"),sQuery(id+"F21.wireOp",EDGE,"E72"),sQuery(id+"F21.wireOp",EDGE,"E73"),sQuery(id+"F21.wireOp",EDGE,"E74"),sQuery(id+"F21.wireOp",EDGE,"E75"),sQuery(id+"F21.wireOp",EDGE,"E76"),sQuery(id+"F21.wireOp",EDGE,"E77"),sQuery(id+"F21.wireOp",EDGE,"E78"),sQuery(id+"F21.wireOp",EDGE,"E79"),sQuery(id+"F21.wireOp",EDGE,"E80"),sQuery(id+"F21.wireOp",EDGE,"E81"),sQuery(id+"F21.wireOp",EDGE,"E82"),sQuery(id+"F21.wireOp",EDGE,"E83"),sQuery(id+"F21.wireOp",EDGE,"E84"),sQuery(id+"F21.wireOp",EDGE,"E85"),sQuery(id+"F21.wireOp",EDGE,"E86"),sQuery(id+"F21.wireOp",EDGE,"E87"),sQuery(id+"F21.wireOp",EDGE,"E88"),sQuery(id+"F21.wireOp",EDGE,"E89.bottom"),sQuery(id+"F21.wireOp",EDGE,"E89.top"),sQuery(id+"F21.wireOp",EDGE,"E89.left"),sQuery(id+"F21.wireOp",EDGE,"E90")])],"isStart":false});
            var sketch = newSketch(context, id + "F25", { "sketchPlane" : qUnion([Q0])});
            skLineSegment(sketch, "E93.top", {"start": v(-3.76, 75) * mm, "end": v(0, 75) * mm});
            skLineSegment(sketch, "E93.left", {"start": v(-3.76, 59.85) * mm, "end": v(-3.76, 75) * mm});
            skLineSegment(sketch, "E93.right", {"start": v(0, 59.85) * mm, "end": v(0, 75) * mm});
            skLineSegment(sketch, "E94.bottom", {"start": v(-3.76, -59.92) * mm, "end": v(0, -59.92) * mm});
            skLineSegment(sketch, "E94.top", {"start": v(-3.76, -75) * mm, "end": v(0, -75) * mm});
            skLineSegment(sketch, "E94.left", {"start": v(-3.76, -59.92) * mm, "end": v(-3.76, -75) * mm});
            skLineSegment(sketch, "E94.right", {"start": v(0, -59.92) * mm, "end": v(0, -75) * mm});
            skLineSegment(sketch, "E95.bottom", {"start": v(-2.85, 66.91) * mm, "end": v(-1.02, 66.91) * mm});
            skLineSegment(sketch, "E95.top", {"start": v(-2.85, 59.26) * mm, "end": v(-1.02, 59.26) * mm});
            skLineSegment(sketch, "E95.left", {"start": v(-2.85, 66.91) * mm, "end": v(-2.85, 59.26) * mm});
            skLineSegment(sketch, "E95.right", {"start": v(-1.02, 66.91) * mm, "end": v(-1.02, 59.26) * mm});
            skLineSegment(sketch, "E96.bottom", {"start": v(-2.97, -58.8) * mm, "end": v(-1, -58.8) * mm});
            skLineSegment(sketch, "E96.top", {"start": v(-2.97, -68.56) * mm, "end": v(-1, -68.56) * mm});
            skLineSegment(sketch, "E96.left", {"start": v(-2.97, -58.8) * mm, "end": v(-2.97, -68.56) * mm});
            skLineSegment(sketch, "E96.right", {"start": v(-1, -58.8) * mm, "end": v(-1, -68.56) * mm});
            skSolve(sketch);
        }
        {
            var Q0;
            Q0 = qSketchRegion(id + "F25", true);
            extrude(context, id + "F26", {"entities" : qUnion([Q0]), "operationType" : NewBodyOperationType.ADD, "oppositeDirection" : true, "depth" : 19.3 * mm, "offsetDistance" : 25.4 * mm});
        }
        {
            var Q0;
            Q0=qCreatedBy(makeId("Right.planeOp"),FACE);
            var sketch = newSketch(context, id + "F27", { "sketchPlane" : qUnion([Q0])});
            skLineSegment(sketch, "E97.bottom", {"start": v(-59.6, 11.15) * mm, "end": v(59.04, 11.15) * mm});
            skLineSegment(sketch, "E97.top", {"start": v(-59.6, 120.66) * mm, "end": v(59.04, 120.66) * mm});
            skLineSegment(sketch, "E97.left", {"start": v(-59.6, 11.15) * mm, "end": v(-59.6, 120.66) * mm});
            skLineSegment(sketch, "E97.right", {"start": v(59.04, 11.15) * mm, "end": v(59.04, 120.66) * mm});
            skSolve(sketch);
        }
        {
            var Q0;
            Q0 = qSketchRegion(id + "F27", true);
            extrude(context, id + "F28", {"entities" : qUnion([Q0]), "operationType" : NewBodyOperationType.ADD, "oppositeDirection" : true, "depth" : 3.8 * mm, "offsetDistance" : 25.4 * mm});
        }
        {
            var Q0;
            Q0=makeQuery(id+"F28.opExtrude","CAP_FACE",FACE,{"disambiguationData":[OSD([sQuery(id+"F27.wireOp",EDGE,"E97.bottom"),sQuery(id+"F27.wireOp",EDGE,"E97.top"),sQuery(id+"F27.wireOp",EDGE,"E97.left"),sQuery(id+"F27.wireOp",EDGE,"E97.right")])],"isStart":true});
            var sketch = newSketch(context, id + "F29", { "sketchPlane" : qUnion([Q0])});
            skLineSegment(sketch, "E98.bottom", {"start": v(-46.71, 120.66) * mm, "end": v(47.2, 120.66) * mm});
            skLineSegment(sketch, "E98.top", {"start": v(-46.71, 109.79) * mm, "end": v(47.2, 109.79) * mm});
            skLineSegment(sketch, "E98.left", {"start": v(-46.71, 120.66) * mm, "end": v(-46.71, 109.79) * mm});
            skLineSegment(sketch, "E98.right", {"start": v(47.2, 120.66) * mm, "end": v(47.2, 109.79) * mm});
            skSolve(sketch);
        }
        {
            var Q0;
            Q0 = qSketchRegion(id + "F29", true);
            extrude(context, id + "F30", {"entities" : qUnion([Q0]), "operationType" : NewBodyOperationType.ADD, "depth" : 25.4 * mm, "offsetDistance" : 25.4 * mm});
        }
        {
            var Q0;
            Q0=makeQuery(id+"F24.opExtrude","CAP_FACE",FACE,{"disambiguationData":[OSD([sQuery(id+"F23.wireOp",EDGE,"E91"),sQuery(id+"F23.wireOp",EDGE,"E92")])],"isStart":false});
            var sketch = newSketch(context, id + "F31", { "sketchPlane" : qUnion([Q0])});
            skLineSegment(sketch, "E99.bottom", {"start": v(-3.7, 59.79) * mm, "end": v(0, 59.79) * mm});
            skLineSegment(sketch, "E99.top", {"start": v(-3.7, 77.58) * mm, "end": v(0, 77.58) * mm});
            skLineSegment(sketch, "E99.left", {"start": v(-3.7, 59.79) * mm, "end": v(-3.7, 77.58) * mm});
            skLineSegment(sketch, "E99.right", {"start": v(0, 59.79) * mm, "end": v(0, 77.58) * mm});
            skLineSegment(sketch, "E100.bottom", {"start": v(-4, -59.53) * mm, "end": v(0, -59.53) * mm});
            skLineSegment(sketch, "E100.top", {"start": v(-4, -77.69) * mm, "end": v(0, -77.69) * mm});
            skLineSegment(sketch, "E100.left", {"start": v(-4, -59.53) * mm, "end": v(-4, -77.69) * mm});
            skLineSegment(sketch, "E100.right", {"start": v(0, -59.53) * mm, "end": v(0, -77.69) * mm});
            skSolve(sketch);
        }
        {
            var Q0;
            Q0 = qSketchRegion(id + "F31", true);
            extrude(context, id + "F32", {"entities" : qUnion([Q0]), "operationType" : NewBodyOperationType.ADD, "oppositeDirection" : true, "depth" : 109.22 * mm, "offsetDistance" : 25.4 * mm});
        }
        {
            var Q0;
            Q0=qCreatedBy(makeId("Top.planeOp"),FACE);
            cPlane(context, id + "F33", {"entities" : qUnion([Q0]), "cplaneType" : CPlaneType.OFFSET, "offset" : 137.16 * mm, "width" : 152.4 * mm, "height" : 152.4 * mm});
        }
        {
            var Q0;
            Q0=qCreatedBy(id+"F33.planeOp",FACE);
            var sketch = newSketch(context, id + "F34", { "sketchPlane" : qUnion([Q0])});
            skArc(sketch, "E101", {"start": v(-4.08, 74.6) * mm, "mid": v(-74.52, 0.48) * mm, "end": v(-4.08, -73.65) * mm});
            skLineSegment(sketch, "E102", {"start": v(-4.08, 74.6) * mm, "end": v(-4.08, -73.65) * mm});
            skSolve(sketch);
        }
        {
            var Q0;
            Q0 = qSketchRegion(id + "F34", true);
            extrude(context, id + "F35", {"entities" : qUnion([Q0]), "depth" : 5.08 * mm, "offsetDistance" : 25.4 * mm});
        }
        {
            var Q0;
            Q0=makeQuery(id+"F35.opExtrude","CAP_FACE",FACE,{"disambiguationData":[OSD([sQuery(id+"F34.wireOp",EDGE,"E101"),sQuery(id+"F34.wireOp",EDGE,"E102")])],"isStart":false});
            var sketch = newSketch(context, id + "F36", { "sketchPlane" : qUnion([Q0])});
            skCircle(sketch, "E103", {"center": v(-35.73, 0) * mm, "radius": 10.8 * mm});
            skSolve(sketch);
        }
        {
            var Q0;
            Q0 = qSketchRegion(id + "F36", true);
            extrude(context, id + "F37", {"entities" : qUnion([Q0]), "operationType" : NewBodyOperationType.ADD, "depth" : 71.12 * mm, "offsetDistance" : 25.4 * mm});
        }
        {
            var Q0;
            Q0=makeQuery(id+"F37.opExtrude","CAP_FACE",FACE,{"disambiguationData":[OSD([sQuery(id+"F36.wireOp",EDGE,"E103")])],"isStart":false});
            var sketch = newSketch(context, id + "F38", { "sketchPlane" : qUnion([Q0])});
            skLineSegment(sketch, "E104", {"start": v(-35.49, -18.92) * mm, "end": v(-35.49, 29.15) * mm, "construction": true});
            skArc(sketch, "E105", {"start": v(-35.49, -18.92) * mm, "mid": v(-16.8, 0) * mm, "end": v(-35.49, 18.92) * mm});
            skSolve(sketch);
        }
        {
            var Q0;
            Q0 = qSketchRegion(id + "F38", true);
            var Q1;
            Q1=sQuery(id+"F38.wireOp",EDGE,"E105");
            var Q2;
            Q2=sQuery(id+"F38.wireOp",EDGE,"E104");
            revolve(context, id + "F39", {"bodyType" : ToolBodyType.SURFACE, "entities" : qUnion([Q0]), "surfaceEntities" : qUnion([Q1]), "axis" : qUnion([Q2]), "revolveType" : RevolveType.FULL});
        }
        {
            var Q0;
            Q0=qCreatedBy(makeId("Top.planeOp"),FACE);
            cPlane(context, id + "F40", {"entities" : qUnion([Q0]), "cplaneType" : CPlaneType.OFFSET, "offset" : 259.08 * mm, "width" : 152.4 * mm, "height" : 152.4 * mm});
        }
        {
            var Q0;
            Q0=qCreatedBy(id+"F40.planeOp",FACE);
            var sketch = newSketch(context, id + "F41", { "sketchPlane" : qUnion([Q0])});
            skCircle(sketch, "E106", {"center": v(0, 0) * mm, "radius": 80 * mm});
            skCircle(sketch, "E107", {"center": v(0, 0) * mm, "radius": 82.5 * mm});
            skSolve(sketch);
        }
        {
            var Q0;
            Q0 = qSketchRegion(id + "F41", true);
            extrude(context, id + "F42", {"entities" : qUnion([Q0]), "oppositeDirection" : true, "depth" : 25.4 * mm, "offsetDistance" : 25.4 * mm});
        }
        {
            var Q0;
            Q0=makeQuery(id+"F42.opExtrude","CAP_FACE",FACE,{"disambiguationData":[OSD([sQuery(id+"F41.wireOp",EDGE,"E106"),sQuery(id+"F41.wireOp",EDGE,"E107")])],"isStart":true});
            var sketch = newSketch(context, id + "F43", { "sketchPlane" : qUnion([Q0])});
            skCircle(sketch, "E108", {"center": v(0, 0) * mm, "radius": 82.5 * mm});
            skSolve(sketch);
        }
        {
            var Q0;
            Q0 = qSketchRegion(id + "F43", true);
            extrude(context, id + "F44", {"entities" : qUnion([Q0]), "operationType" : NewBodyOperationType.ADD, "oppositeDirection" : true, "depth" : 5.08 * mm, "offsetDistance" : 25.4 * mm});
        }
        {
            var Q0;
            Q0=qCreatedBy(makeId("Front.planeOp"),FACE);
            var sketch = newSketch(context, id + "F45", { "sketchPlane" : qUnion([Q0])});
            skArc(sketch, "E109", {"start": v(-40.88, 258.47) * mm, "mid": v(-0.46, 302.03) * mm, "end": v(40.93, 259.4) * mm});
            skArc(sketch, "E110", {"start": v(-33.96, 258.47) * mm, "mid": v(-1.3, 295.1) * mm, "end": v(34.06, 261.07) * mm});
            skLineSegment(sketch, "E111", {"start": v(-40.88, 258.47) * mm, "end": v(-33.96, 258.47) * mm});
            skLineSegment(sketch, "E112", {"start": v(40.93, 259.4) * mm, "end": v(34.06, 259.4) * mm});
            skLineSegment(sketch, "E113", {"start": v(34.06, 259.4) * mm, "end": v(34.06, 261.07) * mm});
            skSolve(sketch);
        }
        {
            var Q0;
            Q0 = qSketchRegion(id + "F45", true);
            extrude(context, id + "F46", {"entities" : qUnion([Q0]), "operationType" : NewBodyOperationType.ADD, "endBound" : BoundingType.SYMMETRIC, "depth" : 25.4 * mm, "offsetDistance" : 25.4 * mm});
        }
        {
            var Q0;
            Q0=makeQuery(id+"F46.opExtrude","CAP_EDGE",EDGE,{"disambiguationData":[OSD([sQuery(id+"F45.wireOp",EDGE,"E109")])],"isStart":false});
            var Q1;
            Q1=makeQuery(id+"F46.opExtrude","CAP_EDGE",EDGE,{"disambiguationData":[OSD([sQuery(id+"F45.wireOp",EDGE,"E109")])],"isStart":true});
            fillet(context, id + "F47", {"entities" : qUnion([Q0, Q1]), "radius" : 5.08 * mm, "tangentPropagation" : true, "allowEdgeOverflow" : false});
        }
    });
